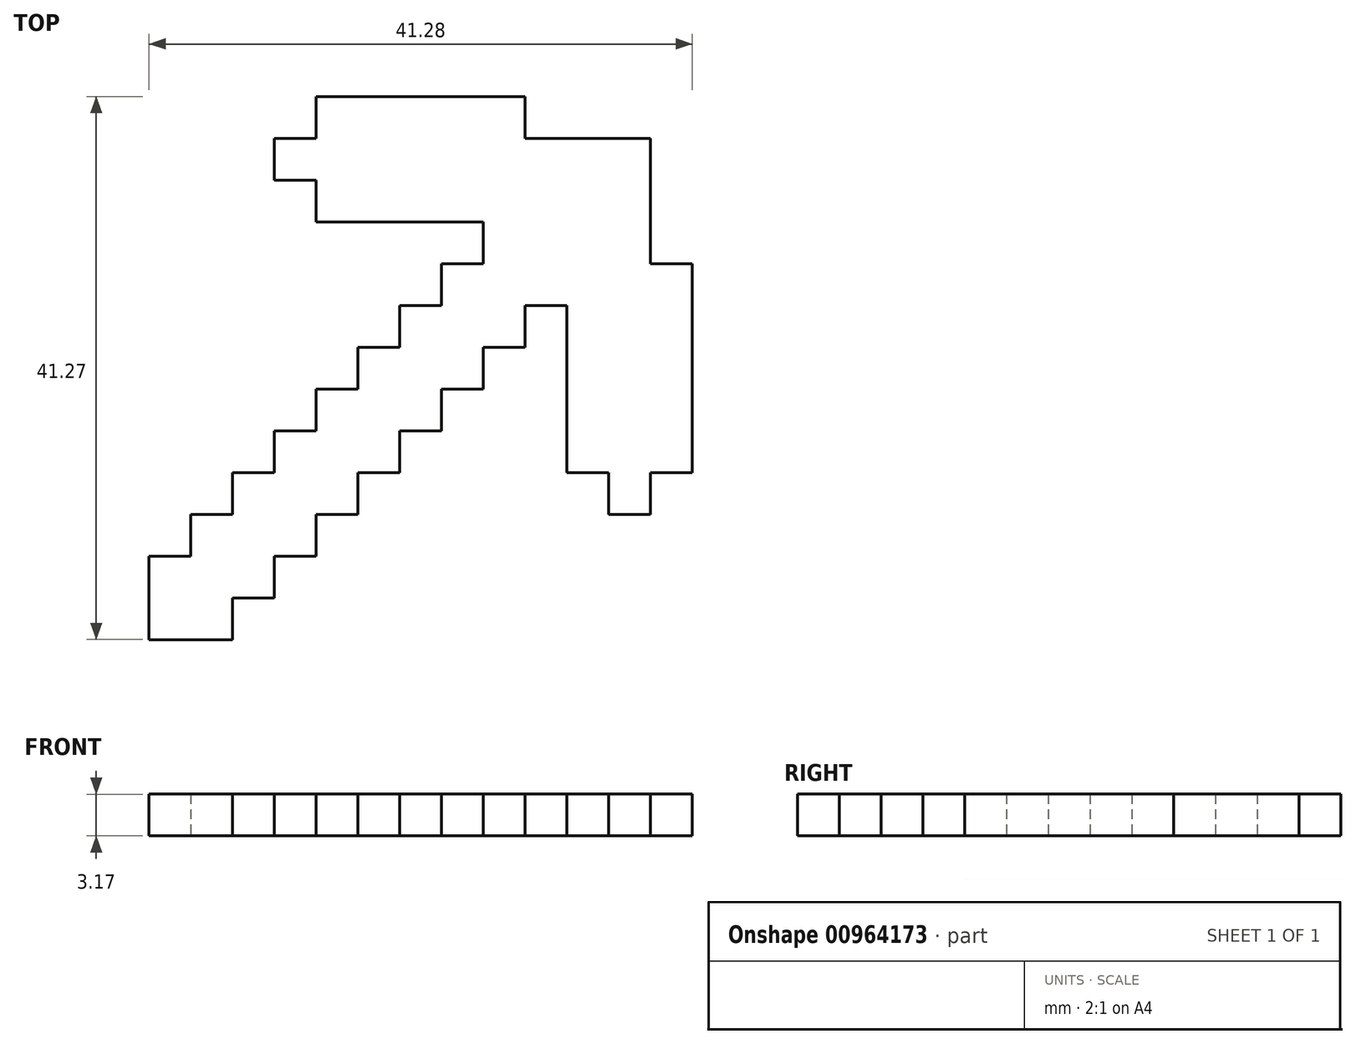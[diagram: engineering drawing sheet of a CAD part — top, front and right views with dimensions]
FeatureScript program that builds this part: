
annotation { "Feature Type Name" : "Feature", "Feature Type Description" : "" }
export const myFeature = defineFeature(function(context is Context, id is Id, definition is map)
    precondition{}
    {
        {
            var Q0;
            Q0=qCreatedBy(makeId("Top.planeOp"),FACE);
            var sketch = newSketch(context, id + "F0", { "sketchPlane" : qUnion([Q0])});
            skLineSegment(sketch, "E0.bottom", {"start": v(-12.64, 16.97) * mm, "end": v(0.06, 16.97) * mm});
            skLineSegment(sketch, "E0.top", {"start": v(-12.64, 4.27) * mm, "end": v(0.06, 4.27) * mm});
            skLineSegment(sketch, "E0.left", {"start": v(-12.64, 16.97) * mm, "end": v(-12.64, 4.27) * mm});
            skLineSegment(sketch, "E0.right", {"start": v(0.06, 16.97) * mm, "end": v(0.06, 4.27) * mm});
            skLineSegment(sketch, "E1.bottom", {"start": v(-25.34, 20.14) * mm, "end": v(-9.46, 20.14) * mm});
            skLineSegment(sketch, "E1.top", {"start": v(-25.34, 10.62) * mm, "end": v(-9.46, 10.62) * mm});
            skLineSegment(sketch, "E1.left", {"start": v(-25.34, 20.14) * mm, "end": v(-25.34, 10.62) * mm});
            skLineSegment(sketch, "E1.right", {"start": v(-9.46, 20.14) * mm, "end": v(-9.46, 10.62) * mm});
            skLineSegment(sketch, "E2.bottom", {"start": v(-28.51, 16.97) * mm, "end": v(-25.08, 16.97) * mm});
            skLineSegment(sketch, "E2.top", {"start": v(-28.51, 13.8) * mm, "end": v(-25.08, 13.8) * mm});
            skLineSegment(sketch, "E2.left", {"start": v(-28.51, 16.97) * mm, "end": v(-28.51, 13.8) * mm});
            skLineSegment(sketch, "E2.right", {"start": v(-25.08, 16.97) * mm, "end": v(-25.08, 13.8) * mm});
            skLineSegment(sketch, "E3.bottom", {"start": v(-6.29, -8.43) * mm, "end": v(-6.29, 7.44) * mm});
            skLineSegment(sketch, "E3.top", {"start": v(3.24, -8.43) * mm, "end": v(3.24, 7.44) * mm});
            skLineSegment(sketch, "E3.left", {"start": v(-6.29, -8.43) * mm, "end": v(3.24, -8.43) * mm});
            skLineSegment(sketch, "E3.right", {"start": v(-6.29, 7.44) * mm, "end": v(3.24, 7.44) * mm});
            skLineSegment(sketch, "E4.bottom", {"start": v(-3.11, -11.6) * mm, "end": v(-3.11, -8.18) * mm});
            skLineSegment(sketch, "E4.top", {"start": v(0.06, -11.6) * mm, "end": v(0.06, -8.18) * mm});
            skLineSegment(sketch, "E4.left", {"start": v(-3.11, -11.6) * mm, "end": v(0.06, -11.6) * mm});
            skLineSegment(sketch, "E4.right", {"start": v(-3.11, -8.18) * mm, "end": v(0.06, -8.18) * mm});
            skLineSegment(sketch, "E5.bottom", {"start": v(-15.81, 7.44) * mm, "end": v(-9.46, 7.44) * mm});
            skLineSegment(sketch, "E5.top", {"start": v(-15.81, 1.1) * mm, "end": v(-9.46, 1.1) * mm});
            skLineSegment(sketch, "E5.left", {"start": v(-15.81, 7.44) * mm, "end": v(-15.81, 1.1) * mm});
            skLineSegment(sketch, "E5.right", {"start": v(-9.46, 7.44) * mm, "end": v(-9.46, 1.1) * mm});
            skLineSegment(sketch, "E6.bottom", {"start": v(-18.99, 4.27) * mm, "end": v(-12.64, 4.27) * mm});
            skLineSegment(sketch, "E6.top", {"start": v(-18.99, -2.08) * mm, "end": v(-12.64, -2.08) * mm});
            skLineSegment(sketch, "E6.left", {"start": v(-18.99, 4.27) * mm, "end": v(-18.99, -2.08) * mm});
            skLineSegment(sketch, "E6.right", {"start": v(-12.64, 4.27) * mm, "end": v(-12.64, -2.08) * mm});
            skLineSegment(sketch, "E7.bottom", {"start": v(-22.16, 1.1) * mm, "end": v(-15.81, 1.1) * mm});
            skLineSegment(sketch, "E7.top", {"start": v(-22.16, -5.26) * mm, "end": v(-15.81, -5.26) * mm});
            skLineSegment(sketch, "E7.left", {"start": v(-22.16, 1.1) * mm, "end": v(-22.16, -5.26) * mm});
            skLineSegment(sketch, "E7.right", {"start": v(-15.81, 1.1) * mm, "end": v(-15.81, -5.26) * mm});
            skLineSegment(sketch, "E8.bottom", {"start": v(-25.34, -2.08) * mm, "end": v(-18.99, -2.08) * mm});
            skLineSegment(sketch, "E8.top", {"start": v(-25.34, -8.43) * mm, "end": v(-18.99, -8.43) * mm});
            skLineSegment(sketch, "E8.left", {"start": v(-25.34, -2.08) * mm, "end": v(-25.34, -8.43) * mm});
            skLineSegment(sketch, "E8.right", {"start": v(-18.99, -2.08) * mm, "end": v(-18.99, -8.43) * mm});
            skLineSegment(sketch, "E9.bottom", {"start": v(-28.51, -5.26) * mm, "end": v(-22.16, -5.26) * mm});
            skLineSegment(sketch, "E9.top", {"start": v(-28.51, -11.6) * mm, "end": v(-22.16, -11.6) * mm});
            skLineSegment(sketch, "E9.left", {"start": v(-28.51, -5.26) * mm, "end": v(-28.51, -11.6) * mm});
            skLineSegment(sketch, "E9.right", {"start": v(-22.16, -5.26) * mm, "end": v(-22.16, -11.6) * mm});
            skLineSegment(sketch, "E10.bottom", {"start": v(-31.69, -8.43) * mm, "end": v(-25.34, -8.43) * mm});
            skLineSegment(sketch, "E10.top", {"start": v(-31.69, -14.78) * mm, "end": v(-25.34, -14.78) * mm});
            skLineSegment(sketch, "E10.left", {"start": v(-31.69, -8.43) * mm, "end": v(-31.69, -14.78) * mm});
            skLineSegment(sketch, "E10.right", {"start": v(-25.34, -8.43) * mm, "end": v(-25.34, -14.78) * mm});
            skLineSegment(sketch, "E11.bottom", {"start": v(-34.86, -11.6) * mm, "end": v(-28.51, -11.6) * mm});
            skLineSegment(sketch, "E11.top", {"start": v(-34.86, -17.96) * mm, "end": v(-28.51, -17.96) * mm});
            skLineSegment(sketch, "E11.left", {"start": v(-34.86, -11.6) * mm, "end": v(-34.86, -17.96) * mm});
            skLineSegment(sketch, "E11.right", {"start": v(-28.51, -11.6) * mm, "end": v(-28.51, -17.96) * mm});
            skLineSegment(sketch, "E12.bottom", {"start": v(-38.04, -14.78) * mm, "end": v(-31.69, -14.78) * mm});
            skLineSegment(sketch, "E12.top", {"start": v(-38.04, -21.13) * mm, "end": v(-31.69, -21.13) * mm});
            skLineSegment(sketch, "E12.left", {"start": v(-38.04, -14.78) * mm, "end": v(-38.04, -21.13) * mm});
            skLineSegment(sketch, "E12.right", {"start": v(-31.69, -14.78) * mm, "end": v(-31.69, -21.13) * mm});
            skSolve(sketch);
        }
        {
            var Q0;
            {var subQ3=sQuery(id+"F0.wireOp",EDGE,"E5.right");var subQ5=sQuery(id+"F0.wireOp",EDGE,"E5.bottom");var subQ7=makeQuery(id+"F0.imprint","INTERSECT",VERTEX,{"derivedFrom":[subQ5,subQ3]});Q0=makeQuery(id+"F0.imprint","IMPRINT",FACE,{"disambiguationData":[TD([[makeQuery(id+"F0.imprint","IMPRINT",EDGE,{"disambiguationData":[TD([[subQ7,1.0]])],"derivedFrom":subQ5}),-1.0]])]});}
            var Q1;
            {var subQ3=sQuery(id+"F0.wireOp",EDGE,"E9.right");var subQ5=sQuery(id+"F0.wireOp",EDGE,"E9.top");var subQ7=makeQuery(id+"F0.imprint","INTERSECT",VERTEX,{"derivedFrom":[subQ5,subQ3]});Q1=makeQuery(id+"F0.imprint","IMPRINT",FACE,{"disambiguationData":[TD([[makeQuery(id+"F0.imprint","IMPRINT",EDGE,{"disambiguationData":[TD([[subQ7,1.0]])],"derivedFrom":subQ5}),1.0]])]});}
            var Q2;
            {var subQ1=sQuery(id+"F0.wireOp",EDGE,"E7.top");var subQ3=sQuery(id+"F0.wireOp",EDGE,"E8.right");var subQ4=makeQuery(id+"F0.imprint","INTERSECT",VERTEX,{"derivedFrom":[subQ1,subQ3]});Q2=makeQuery(id+"F0.imprint","IMPRINT",FACE,{"disambiguationData":[TD([[makeQuery(id+"F0.imprint","IMPRINT",EDGE,{"disambiguationData":[TD([[subQ4,1.0]])],"derivedFrom":subQ1}),1.0]])]});}
            var Q3;
            {var subQ0=sQuery(id+"F0.wireOp",EDGE,"E0.right");var subQ1=sQuery(id+"F0.wireOp",EDGE,"E0.bottom");var subQ2=makeQuery(id+"F0.imprint","INTERSECT",VERTEX,{"derivedFrom":[subQ1,subQ0]});Q3=makeQuery(id+"F0.imprint","IMPRINT",FACE,{"disambiguationData":[TD([[makeQuery(id+"F0.imprint","IMPRINT",EDGE,{"disambiguationData":[TD([[subQ2,1.0]])],"derivedFrom":subQ1}),-1.0]])]});}
            var Q4;
            {var subQ1=sQuery(id+"F0.wireOp",EDGE,"E9.top");var subQ3=sQuery(id+"F0.wireOp",EDGE,"E10.right");var subQ4=makeQuery(id+"F0.imprint","INTERSECT",VERTEX,{"derivedFrom":[subQ1,subQ3]});Q4=makeQuery(id+"F0.imprint","IMPRINT",FACE,{"disambiguationData":[TD([[makeQuery(id+"F0.imprint","IMPRINT",EDGE,{"disambiguationData":[TD([[subQ4,1.0]])],"derivedFrom":subQ1}),1.0]])]});}
            var Q5;
            {var subQ3=sQuery(id+"F0.wireOp",EDGE,"E9.bottom");var subQ5=sQuery(id+"F0.wireOp",EDGE,"E9.left");var subQ6=makeQuery(id+"F0.imprint","INTERSECT",VERTEX,{"derivedFrom":[subQ3,subQ5]});Q5=makeQuery(id+"F0.imprint","IMPRINT",FACE,{"disambiguationData":[TD([[makeQuery(id+"F0.imprint","IMPRINT",EDGE,{"disambiguationData":[TD([[subQ6,-1.0]])],"derivedFrom":subQ3}),-1.0]])]});}
            var Q6;
            {var subQ3=sQuery(id+"F0.wireOp",EDGE,"E6.bottom");var subQ5=sQuery(id+"F0.wireOp",EDGE,"E6.left");var subQ6=makeQuery(id+"F0.imprint","INTERSECT",VERTEX,{"derivedFrom":[subQ3,subQ5]});Q6=makeQuery(id+"F0.imprint","IMPRINT",FACE,{"disambiguationData":[TD([[makeQuery(id+"F0.imprint","IMPRINT",EDGE,{"disambiguationData":[TD([[subQ6,-1.0]])],"derivedFrom":subQ3}),-1.0]])]});}
            var Q7;
            {var subQ3=sQuery(id+"F0.wireOp",EDGE,"E11.right");var subQ5=sQuery(id+"F0.wireOp",EDGE,"E11.top");var subQ6=makeQuery(id+"F0.imprint","INTERSECT",VERTEX,{"derivedFrom":[subQ5,subQ3]});Q7=makeQuery(id+"F0.imprint","IMPRINT",FACE,{"disambiguationData":[TD([[makeQuery(id+"F0.imprint","IMPRINT",EDGE,{"disambiguationData":[TD([[subQ6,1.0]])],"derivedFrom":subQ5}),1.0]])]});}
            var Q8;
            {var subQ3=sQuery(id+"F0.wireOp",EDGE,"E6.right");var subQ5=sQuery(id+"F0.wireOp",EDGE,"E6.top");var subQ7=makeQuery(id+"F0.imprint","INTERSECT",VERTEX,{"derivedFrom":[subQ5,subQ3]});Q8=makeQuery(id+"F0.imprint","IMPRINT",FACE,{"disambiguationData":[TD([[makeQuery(id+"F0.imprint","IMPRINT",EDGE,{"disambiguationData":[TD([[subQ7,1.0]])],"derivedFrom":subQ5}),1.0]])]});}
            var Q9;
            {var subQ3=sQuery(id+"F0.wireOp",EDGE,"E5.bottom");var subQ5=sQuery(id+"F0.wireOp",EDGE,"E5.left");var subQ6=makeQuery(id+"F0.imprint","INTERSECT",VERTEX,{"derivedFrom":[subQ3,subQ5]});Q9=makeQuery(id+"F0.imprint","IMPRINT",FACE,{"disambiguationData":[TD([[makeQuery(id+"F0.imprint","IMPRINT",EDGE,{"disambiguationData":[TD([[subQ6,-1.0]])],"derivedFrom":subQ3}),-1.0]])]});}
            var Q10;
            {var subQ0=sQuery(id+"F0.wireOp",EDGE,"E0.right");var subQ1=sQuery(id+"F0.wireOp",EDGE,"E0.top");var subQ2=makeQuery(id+"F0.imprint","INTERSECT",VERTEX,{"derivedFrom":[subQ1,subQ0]});Q10=makeQuery(id+"F0.imprint","IMPRINT",FACE,{"disambiguationData":[TD([[makeQuery(id+"F0.imprint","IMPRINT",EDGE,{"disambiguationData":[TD([[subQ2,1.0]])],"derivedFrom":subQ1}),1.0]])]});}
            var Q11;
            {var subQ3=sQuery(id+"F0.wireOp",EDGE,"E5.right");var subQ5=sQuery(id+"F0.wireOp",EDGE,"E5.top");var subQ7=makeQuery(id+"F0.imprint","INTERSECT",VERTEX,{"derivedFrom":[subQ5,subQ3]});Q11=makeQuery(id+"F0.imprint","IMPRINT",FACE,{"disambiguationData":[TD([[makeQuery(id+"F0.imprint","IMPRINT",EDGE,{"disambiguationData":[TD([[subQ7,1.0]])],"derivedFrom":subQ5}),1.0]])]});}
            var Q12;
            {var subQ0=sQuery(id+"F0.wireOp",EDGE,"E3.top");Q12=makeQuery(id+"F0.imprint","IMPRINT",FACE,{"disambiguationData":[TD([[makeQuery(id+"F0.imprint","IMPRINT",EDGE,{"derivedFrom":subQ0}),1.0]])]});}
            var Q13;
            {var subQ0=sQuery(id+"F0.wireOp",EDGE,"E0.left");var subQ1=sQuery(id+"F0.wireOp",EDGE,"E0.bottom");var subQ2=makeQuery(id+"F0.imprint","INTERSECT",VERTEX,{"derivedFrom":[subQ1,subQ0]});Q13=makeQuery(id+"F0.imprint","IMPRINT",FACE,{"disambiguationData":[TD([[makeQuery(id+"F0.imprint","IMPRINT",EDGE,{"disambiguationData":[TD([[subQ2,-1.0]])],"derivedFrom":subQ1}),-1.0]])]});}
            var Q14;
            {var subQ9=sQuery(id+"F0.wireOp",EDGE,"E1.bottom");Q14=makeQuery(id+"F0.imprint","IMPRINT",FACE,{"disambiguationData":[TD([[makeQuery(id+"F0.imprint","IMPRINT",EDGE,{"derivedFrom":subQ9}),-1.0]])]});}
            var Q15;
            {var subQ4=sQuery(id+"F0.wireOp",EDGE,"E12.top");Q15=makeQuery(id+"F0.imprint","IMPRINT",FACE,{"disambiguationData":[TD([[makeQuery(id+"F0.imprint","IMPRINT",EDGE,{"derivedFrom":subQ4}),1.0]])]});}
            var Q16;
            {var subQ5=sQuery(id+"F0.wireOp",EDGE,"E4.left");Q16=makeQuery(id+"F0.imprint","IMPRINT",FACE,{"disambiguationData":[TD([[makeQuery(id+"F0.imprint","IMPRINT",EDGE,{"derivedFrom":subQ5}),1.0]])]});}
            var Q17;
            {var subQ5=sQuery(id+"F0.wireOp",EDGE,"E2.left");Q17=makeQuery(id+"F0.imprint","IMPRINT",FACE,{"disambiguationData":[TD([[makeQuery(id+"F0.imprint","IMPRINT",EDGE,{"derivedFrom":subQ5}),1.0]])]});}
            var Q18;
            {var subQ3=sQuery(id+"F0.wireOp",EDGE,"E8.bottom");var subQ5=sQuery(id+"F0.wireOp",EDGE,"E8.left");var subQ6=makeQuery(id+"F0.imprint","INTERSECT",VERTEX,{"derivedFrom":[subQ3,subQ5]});Q18=makeQuery(id+"F0.imprint","IMPRINT",FACE,{"disambiguationData":[TD([[makeQuery(id+"F0.imprint","IMPRINT",EDGE,{"disambiguationData":[TD([[subQ6,-1.0]])],"derivedFrom":subQ3}),-1.0]])]});}
            var Q19;
            {var subQ3=sQuery(id+"F0.wireOp",EDGE,"E7.bottom");var subQ5=sQuery(id+"F0.wireOp",EDGE,"E7.left");var subQ6=makeQuery(id+"F0.imprint","INTERSECT",VERTEX,{"derivedFrom":[subQ3,subQ5]});Q19=makeQuery(id+"F0.imprint","IMPRINT",FACE,{"disambiguationData":[TD([[makeQuery(id+"F0.imprint","IMPRINT",EDGE,{"disambiguationData":[TD([[subQ6,-1.0]])],"derivedFrom":subQ3}),-1.0]])]});}
            var Q20;
            {var subQ3=sQuery(id+"F0.wireOp",EDGE,"E7.right");var subQ5=sQuery(id+"F0.wireOp",EDGE,"E7.top");var subQ7=makeQuery(id+"F0.imprint","INTERSECT",VERTEX,{"derivedFrom":[subQ5,subQ3]});Q20=makeQuery(id+"F0.imprint","IMPRINT",FACE,{"disambiguationData":[TD([[makeQuery(id+"F0.imprint","IMPRINT",EDGE,{"disambiguationData":[TD([[subQ7,1.0]])],"derivedFrom":subQ5}),1.0]])]});}
            var Q21;
            {var subQ1=sQuery(id+"F0.wireOp",EDGE,"E6.top");var subQ3=sQuery(id+"F0.wireOp",EDGE,"E7.right");var subQ4=makeQuery(id+"F0.imprint","INTERSECT",VERTEX,{"derivedFrom":[subQ1,subQ3]});Q21=makeQuery(id+"F0.imprint","IMPRINT",FACE,{"disambiguationData":[TD([[makeQuery(id+"F0.imprint","IMPRINT",EDGE,{"disambiguationData":[TD([[subQ4,1.0]])],"derivedFrom":subQ1}),1.0]])]});}
            var Q22;
            {var subQ3=sQuery(id+"F0.wireOp",EDGE,"E8.right");var subQ5=sQuery(id+"F0.wireOp",EDGE,"E8.top");var subQ7=makeQuery(id+"F0.imprint","INTERSECT",VERTEX,{"derivedFrom":[subQ5,subQ3]});Q22=makeQuery(id+"F0.imprint","IMPRINT",FACE,{"disambiguationData":[TD([[makeQuery(id+"F0.imprint","IMPRINT",EDGE,{"disambiguationData":[TD([[subQ7,1.0]])],"derivedFrom":subQ5}),1.0]])]});}
            var Q23;
            {var subQ3=sQuery(id+"F0.wireOp",EDGE,"E11.bottom");var subQ5=sQuery(id+"F0.wireOp",EDGE,"E11.left");var subQ6=makeQuery(id+"F0.imprint","INTERSECT",VERTEX,{"derivedFrom":[subQ3,subQ5]});Q23=makeQuery(id+"F0.imprint","IMPRINT",FACE,{"disambiguationData":[TD([[makeQuery(id+"F0.imprint","IMPRINT",EDGE,{"disambiguationData":[TD([[subQ6,-1.0]])],"derivedFrom":subQ3}),-1.0]])]});}
            var Q24;
            {var subQ1=sQuery(id+"F0.wireOp",EDGE,"E10.top");var subQ3=sQuery(id+"F0.wireOp",EDGE,"E11.right");var subQ4=makeQuery(id+"F0.imprint","INTERSECT",VERTEX,{"derivedFrom":[subQ1,subQ3]});Q24=makeQuery(id+"F0.imprint","IMPRINT",FACE,{"disambiguationData":[TD([[makeQuery(id+"F0.imprint","IMPRINT",EDGE,{"disambiguationData":[TD([[subQ4,1.0]])],"derivedFrom":subQ1}),1.0]])]});}
            var Q25;
            {var subQ1=sQuery(id+"F0.wireOp",EDGE,"E8.top");var subQ3=sQuery(id+"F0.wireOp",EDGE,"E9.right");var subQ4=makeQuery(id+"F0.imprint","INTERSECT",VERTEX,{"derivedFrom":[subQ1,subQ3]});Q25=makeQuery(id+"F0.imprint","IMPRINT",FACE,{"disambiguationData":[TD([[makeQuery(id+"F0.imprint","IMPRINT",EDGE,{"disambiguationData":[TD([[subQ4,1.0]])],"derivedFrom":subQ1}),1.0]])]});}
            var Q26;
            {var subQ3=sQuery(id+"F0.wireOp",EDGE,"E10.bottom");var subQ5=sQuery(id+"F0.wireOp",EDGE,"E10.left");var subQ6=makeQuery(id+"F0.imprint","INTERSECT",VERTEX,{"derivedFrom":[subQ3,subQ5]});Q26=makeQuery(id+"F0.imprint","IMPRINT",FACE,{"disambiguationData":[TD([[makeQuery(id+"F0.imprint","IMPRINT",EDGE,{"disambiguationData":[TD([[subQ6,-1.0]])],"derivedFrom":subQ3}),-1.0]])]});}
            var Q27;
            {var subQ1=sQuery(id+"F0.wireOp",EDGE,"E5.top");var subQ3=sQuery(id+"F0.wireOp",EDGE,"E6.right");var subQ4=makeQuery(id+"F0.imprint","INTERSECT",VERTEX,{"derivedFrom":[subQ1,subQ3]});Q27=makeQuery(id+"F0.imprint","IMPRINT",FACE,{"disambiguationData":[TD([[makeQuery(id+"F0.imprint","IMPRINT",EDGE,{"disambiguationData":[TD([[subQ4,1.0]])],"derivedFrom":subQ1}),1.0]])]});}
            var Q28;
            {var subQ0=sQuery(id+"F0.wireOp",EDGE,"E11.left");var subQ1=sQuery(id+"F0.wireOp",EDGE,"E11.top");var subQ2=makeQuery(id+"F0.imprint","INTERSECT",VERTEX,{"derivedFrom":[subQ1,subQ0]});Q28=makeQuery(id+"F0.imprint","IMPRINT",FACE,{"disambiguationData":[TD([[makeQuery(id+"F0.imprint","IMPRINT",EDGE,{"disambiguationData":[TD([[subQ2,-1.0]])],"derivedFrom":subQ1}),1.0]])]});}
            var Q29;
            {var subQ3=sQuery(id+"F0.wireOp",EDGE,"E10.right");var subQ5=sQuery(id+"F0.wireOp",EDGE,"E10.top");var subQ7=makeQuery(id+"F0.imprint","INTERSECT",VERTEX,{"derivedFrom":[subQ5,subQ3]});Q29=makeQuery(id+"F0.imprint","IMPRINT",FACE,{"disambiguationData":[TD([[makeQuery(id+"F0.imprint","IMPRINT",EDGE,{"disambiguationData":[TD([[subQ7,1.0]])],"derivedFrom":subQ5}),1.0]])]});}
            var Q30;
            {var subQ5=sQuery(id+"F0.wireOp",EDGE,"E2.right");Q30=makeQuery(id+"F0.imprint","IMPRINT",FACE,{"disambiguationData":[TD([[makeQuery(id+"F0.imprint","IMPRINT",EDGE,{"derivedFrom":subQ5}),-1.0]])]});}
            var Q31;
            {var subQ5=sQuery(id+"F0.wireOp",EDGE,"E4.right");Q31=makeQuery(id+"F0.imprint","IMPRINT",FACE,{"disambiguationData":[TD([[makeQuery(id+"F0.imprint","IMPRINT",EDGE,{"derivedFrom":subQ5}),-1.0]])]});}
            extrude(context, id + "F1", {"entities" : qUnion([Q0, Q1, Q2, Q3, Q4, Q5, Q6, Q7, Q8, Q9, Q10, Q11, Q12, Q13, Q14, Q15, Q16, Q17, Q18, Q19, Q20, Q21, Q22, Q23, Q24, Q25, Q26, Q27, Q28, Q29, Q30, Q31]), "depth" : 3.17 * mm, "offsetDistance" : 25.4 * mm});
        }
    });
